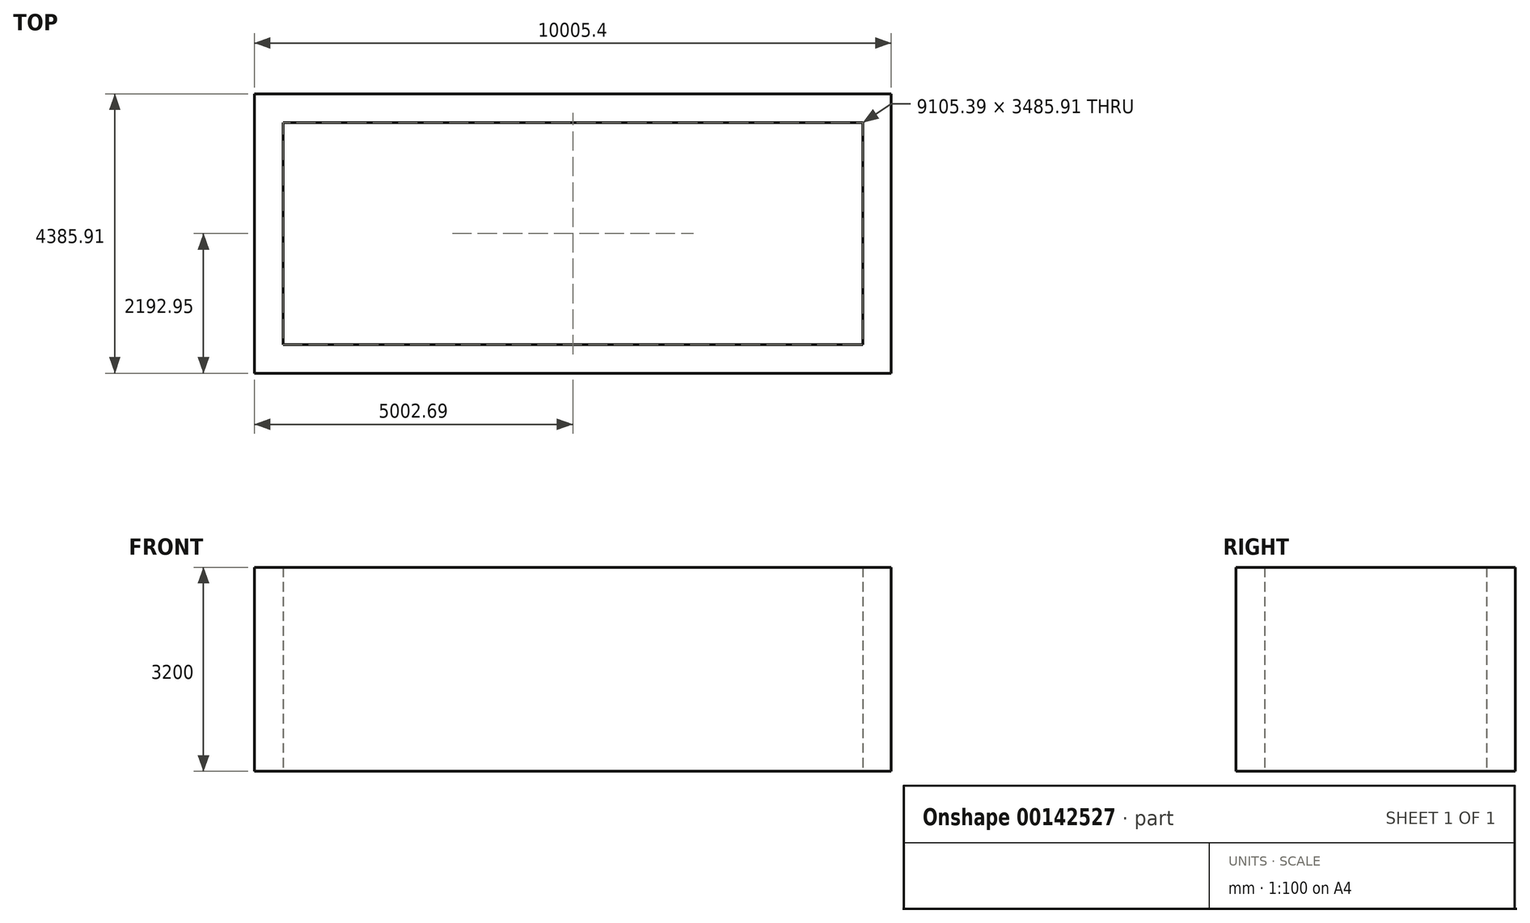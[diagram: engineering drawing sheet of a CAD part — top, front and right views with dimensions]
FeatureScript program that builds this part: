
annotation { "Feature Type Name" : "Feature", "Feature Type Description" : "" }
export const myFeature = defineFeature(function(context is Context, id is Id, definition is map)
    precondition{}
    {
        {
            var Q0;
            Q0=qCreatedBy(makeId("Top.planeOp"),FACE);
            var sketch = newSketch(context, id + "F0", { "sketchPlane" : qUnion([Q0])});
            skLineSegment(sketch, "E0", {"start": v(-343.28, -223.7) * mm, "end": v(9662.1, -223.7) * mm});
            skLineSegment(sketch, "E1", {"start": v(9662.1, -223.7) * mm, "end": v(9662.1, -4609.6) * mm});
            skLineSegment(sketch, "E2", {"start": v(9662.1, -4609.6) * mm, "end": v(-343.28, -4609.6) * mm});
            skLineSegment(sketch, "E3", {"start": v(-343.28, -4609.6) * mm, "end": v(-343.28, -223.7) * mm});
            skLineSegment(sketch, "E4.0", {"start": v(-343.28, -673.7) * mm, "end": v(9662.1, -673.7) * mm});
            skLineSegment(sketch, "E5.0", {"start": v(9662.1, -4159.6) * mm, "end": v(-343.28, -4159.6) * mm});
            skLineSegment(sketch, "E6.0", {"start": v(106.72, -4609.6) * mm, "end": v(106.72, -223.7) * mm});
            skLineSegment(sketch, "E7.0", {"start": v(9212.1, -223.7) * mm, "end": v(9212.1, -4609.6) * mm});
            skSolve(sketch);
        }
        {
            var Q0;
            {var subQ0=sQuery(id+"F0.wireOp",EDGE,"E3");var subQ1=sQuery(id+"F0.wireOp",EDGE,"E0");var subQ2=makeQuery(id+"F0.imprint","INTERSECT",VERTEX,{"derivedFrom":[subQ1,subQ0]});Q0=makeQuery(id+"F0.imprint","IMPRINT",FACE,{"disambiguationData":[TD([[makeQuery(id+"F0.imprint","IMPRINT",EDGE,{"disambiguationData":[TD([[subQ2,-1.0]])],"derivedFrom":subQ1}),-1.0]])]});}
            var Q1;
            {var subQ0=sQuery(id+"F0.wireOp",EDGE,"E1");var subQ1=sQuery(id+"F0.wireOp",EDGE,"E0");var subQ2=makeQuery(id+"F0.imprint","INTERSECT",VERTEX,{"derivedFrom":[subQ1,subQ0]});Q1=makeQuery(id+"F0.imprint","IMPRINT",FACE,{"disambiguationData":[TD([[makeQuery(id+"F0.imprint","IMPRINT",EDGE,{"disambiguationData":[TD([[subQ2,1.0]])],"derivedFrom":subQ1}),-1.0]])]});}
            var Q2;
            {var subQ0=sQuery(id+"F0.wireOp",EDGE,"E2");var subQ1=sQuery(id+"F0.wireOp",EDGE,"E1");var subQ2=makeQuery(id+"F0.imprint","INTERSECT",VERTEX,{"derivedFrom":[subQ1,subQ0]});Q2=makeQuery(id+"F0.imprint","IMPRINT",FACE,{"disambiguationData":[TD([[makeQuery(id+"F0.imprint","IMPRINT",EDGE,{"disambiguationData":[TD([[subQ2,1.0]])],"derivedFrom":subQ1}),-1.0]])]});}
            var Q3;
            {var subQ0=sQuery(id+"F0.wireOp",EDGE,"E3");var subQ1=sQuery(id+"F0.wireOp",EDGE,"E2");var subQ2=makeQuery(id+"F0.imprint","INTERSECT",VERTEX,{"derivedFrom":[subQ1,subQ0]});Q3=makeQuery(id+"F0.imprint","IMPRINT",FACE,{"disambiguationData":[TD([[makeQuery(id+"F0.imprint","IMPRINT",EDGE,{"disambiguationData":[TD([[subQ2,1.0]])],"derivedFrom":subQ1}),-1.0]])]});}
            var Q4;
            {var subQ0=sQuery(id+"F0.wireOp",EDGE,"E4.0");var subQ1=sQuery(id+"F0.wireOp",EDGE,"E1");var subQ2=makeQuery(id+"F0.imprint","INTERSECT",VERTEX,{"derivedFrom":[subQ1,subQ0]});Q4=makeQuery(id+"F0.imprint","IMPRINT",FACE,{"disambiguationData":[TD([[makeQuery(id+"F0.imprint","IMPRINT",EDGE,{"disambiguationData":[TD([[subQ2,-1.0]])],"derivedFrom":subQ1}),-1.0]])]});}
            var Q5;
            {var subQ0=sQuery(id+"F0.wireOp",EDGE,"E6.0");var subQ1=sQuery(id+"F0.wireOp",EDGE,"E2");var subQ2=makeQuery(id+"F0.imprint","INTERSECT",VERTEX,{"derivedFrom":[subQ1,subQ0]});Q5=makeQuery(id+"F0.imprint","IMPRINT",FACE,{"disambiguationData":[TD([[makeQuery(id+"F0.imprint","IMPRINT",EDGE,{"disambiguationData":[TD([[subQ2,1.0]])],"derivedFrom":subQ1}),-1.0]])]});}
            var Q6;
            {var subQ0=sQuery(id+"F0.wireOp",EDGE,"E4.0");var subQ1=sQuery(id+"F0.wireOp",EDGE,"E3");var subQ2=makeQuery(id+"F0.imprint","INTERSECT",VERTEX,{"derivedFrom":[subQ1,subQ0]});Q6=makeQuery(id+"F0.imprint","IMPRINT",FACE,{"disambiguationData":[TD([[makeQuery(id+"F0.imprint","IMPRINT",EDGE,{"disambiguationData":[TD([[subQ2,1.0]])],"derivedFrom":subQ1}),-1.0]])]});}
            var Q7;
            {var subQ0=sQuery(id+"F0.wireOp",EDGE,"E6.0");var subQ1=sQuery(id+"F0.wireOp",EDGE,"E0");var subQ2=makeQuery(id+"F0.imprint","INTERSECT",VERTEX,{"derivedFrom":[subQ1,subQ0]});Q7=makeQuery(id+"F0.imprint","IMPRINT",FACE,{"disambiguationData":[TD([[makeQuery(id+"F0.imprint","IMPRINT",EDGE,{"disambiguationData":[TD([[subQ2,-1.0]])],"derivedFrom":subQ1}),-1.0]])]});}
            extrude(context, id + "F1", {"entities" : qUnion([Q0, Q1, Q2, Q3, Q4, Q5, Q6, Q7]), "depth" : 3200 * mm});
        }
    });
